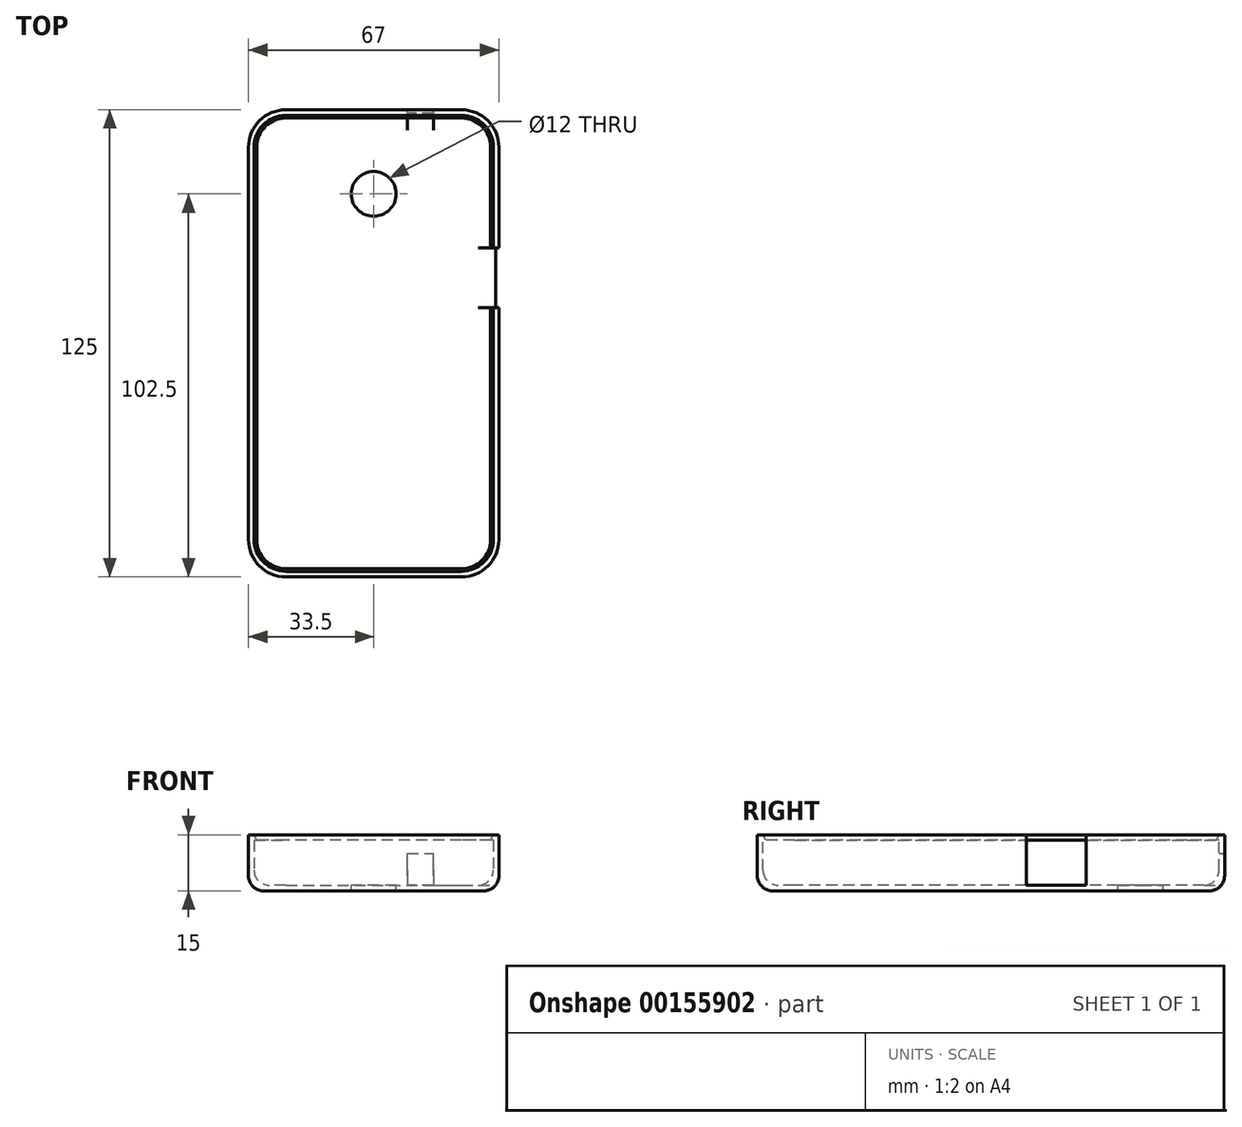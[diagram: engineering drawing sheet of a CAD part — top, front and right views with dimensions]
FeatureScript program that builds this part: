
annotation { "Feature Type Name" : "Feature", "Feature Type Description" : "" }
export const myFeature = defineFeature(function(context is Context, id is Id, definition is map)
    precondition{}
    {
        {
            var Q0;
            Q0=qCreatedBy(makeId("Top.planeOp"),FACE);
            var sketch = newSketch(context, id + "F0", { "sketchPlane" : qUnion([Q0])});
            skLineSegment(sketch, "E0.bottom", {"start": v(-23.5, 62.5) * mm, "end": v(23.5, 62.5) * mm});
            skLineSegment(sketch, "E0.top", {"start": v(-23.5, -62.5) * mm, "end": v(23.5, -62.5) * mm});
            skLineSegment(sketch, "E0.left", {"start": v(-33.5, 52.5) * mm, "end": v(-33.5, -52.5) * mm});
            skLineSegment(sketch, "E0.right", {"start": v(33.5, 52.5) * mm, "end": v(33.5, -52.5) * mm});
            skPoint(sketch, "E1.visualSharp", {"position": v(-33.5, 62.5) * mm});
            skArc(sketch, "E1.filletArc", {"start": v(-23.5, 62.5) * mm, "mid": v(-30.57, 59.57) * mm, "end": v(-33.5, 52.5) * mm});
            skPoint(sketch, "E2.visualSharp", {"position": v(33.5, 62.5) * mm});
            skArc(sketch, "E2.filletArc", {"start": v(33.5, 52.5) * mm, "mid": v(30.57, 59.57) * mm, "end": v(23.5, 62.5) * mm});
            skPoint(sketch, "E3.visualSharp", {"position": v(33.5, -62.5) * mm});
            skArc(sketch, "E3.filletArc", {"start": v(23.5, -62.5) * mm, "mid": v(30.57, -59.57) * mm, "end": v(33.5, -52.5) * mm});
            skPoint(sketch, "E4.visualSharp", {"position": v(-33.5, -62.5) * mm});
            skArc(sketch, "E4.filletArc", {"start": v(-33.5, -52.5) * mm, "mid": v(-30.57, -59.57) * mm, "end": v(-23.5, -62.5) * mm});
            skSolve(sketch);
        }
        {
            var Q0;
            Q0=makeQuery(id+"F0.imprint","IMPRINT",FACE,{"disambiguationData":[TD([[makeQuery(id+"F0.imprint","IMPRINT",EDGE,{"derivedFrom":sQuery(id+"F0.wireOp",EDGE,"E0.bottom")}),-1.0]])]});
            extrude(context, id + "F1", {"entities" : qUnion([Q0]), "depth" : 15 * mm});
        }
        {
            var Q0;
            Q0=makeQuery(id+"F1.opExtrude","CAP_FACE",FACE,{"disambiguationData":[OSD([sQuery(id+"F0.wireOp",EDGE,"E0.bottom"),sQuery(id+"F0.wireOp",EDGE,"E0.top"),sQuery(id+"F0.wireOp",EDGE,"E0.left"),sQuery(id+"F0.wireOp",EDGE,"E0.right"),sQuery(id+"F0.wireOp",EDGE,"E1.filletArc"),sQuery(id+"F0.wireOp",EDGE,"E2.filletArc"),sQuery(id+"F0.wireOp",EDGE,"E3.filletArc"),sQuery(id+"F0.wireOp",EDGE,"E4.filletArc")])],"isStart":false});
            shell(context, id + "F2", {"entities" : qUnion([Q0]), "thickness" : 1.5 * mm});
        }
        {
            var Q0;
            Q0=makeQuery(id+"F2.opShell","OFFSET_FACE",FACE,{"disambiguationData":[OSD([sQuery(id+"F0.wireOp",EDGE,"E0.bottom"),sQuery(id+"F0.wireOp",EDGE,"E0.top"),sQuery(id+"F0.wireOp",EDGE,"E0.left"),sQuery(id+"F0.wireOp",EDGE,"E0.right"),sQuery(id+"F0.wireOp",EDGE,"E1.filletArc"),sQuery(id+"F0.wireOp",EDGE,"E2.filletArc"),sQuery(id+"F0.wireOp",EDGE,"E3.filletArc"),sQuery(id+"F0.wireOp",EDGE,"E4.filletArc")])]});
            var sketch = newSketch(context, id + "F3", { "sketchPlane" : qUnion([Q0])});
            skCircle(sketch, "E5", {"center": v(0, 40) * mm, "radius": 6 * mm});
            skSolve(sketch);
        }
        {
            var Q0;
            Q0=makeQuery(id+"F3.imprint","IMPRINT",FACE,{"disambiguationData":[TD([[makeQuery(id+"F3.imprint","IMPRINT",EDGE,{"derivedFrom":sQuery(id+"F3.wireOp",EDGE,"E5")}),1.0]])]});
            extrude(context, id + "F4", {"entities" : qUnion([Q0]), "operationType" : NewBodyOperationType.REMOVE, "oppositeDirection" : true, "depth" : 25 * mm});
        }
        {
            var Q0;
            {var subQ0=sQuery(id+"F0.wireOp",EDGE,"E0.right");Q0=makeQuery(id+"F2.opShell","OFFSET_EDGE",EDGE,{"disambiguationData":[OSD([subQ0]),TDD([makeQuery(id+"F1.opExtrude","CAP_EDGE",EDGE,{"disambiguationData":[OSD([subQ0])],"isStart":true})])]});}
            var Q1;
            {var subQ0=sQuery(id+"F0.wireOp",EDGE,"E2.filletArc");Q1=makeQuery(id+"F2.opShell","OFFSET_EDGE",EDGE,{"disambiguationData":[OSD([subQ0]),TDD([makeQuery(id+"F1.opExtrude","CAP_EDGE",EDGE,{"disambiguationData":[OSD([subQ0])],"isStart":true})])]});}
            var Q2;
            {var subQ0=sQuery(id+"F0.wireOp",EDGE,"E0.bottom");Q2=makeQuery(id+"F2.opShell","OFFSET_EDGE",EDGE,{"disambiguationData":[OSD([subQ0]),TDD([makeQuery(id+"F1.opExtrude","CAP_EDGE",EDGE,{"disambiguationData":[OSD([subQ0])],"isStart":true})])]});}
            var Q3;
            {var subQ0=sQuery(id+"F0.wireOp",EDGE,"E1.filletArc");Q3=makeQuery(id+"F2.opShell","OFFSET_EDGE",EDGE,{"disambiguationData":[OSD([subQ0]),TDD([makeQuery(id+"F1.opExtrude","CAP_EDGE",EDGE,{"disambiguationData":[OSD([subQ0])],"isStart":true})])]});}
            var Q4;
            {var subQ0=sQuery(id+"F0.wireOp",EDGE,"E0.left");Q4=makeQuery(id+"F2.opShell","OFFSET_EDGE",EDGE,{"disambiguationData":[OSD([subQ0]),TDD([makeQuery(id+"F1.opExtrude","CAP_EDGE",EDGE,{"disambiguationData":[OSD([subQ0])],"isStart":true})])]});}
            var Q5;
            {var subQ0=sQuery(id+"F0.wireOp",EDGE,"E4.filletArc");Q5=makeQuery(id+"F2.opShell","OFFSET_EDGE",EDGE,{"disambiguationData":[OSD([subQ0]),TDD([makeQuery(id+"F1.opExtrude","CAP_EDGE",EDGE,{"disambiguationData":[OSD([subQ0])],"isStart":true})])]});}
            var Q6;
            {var subQ0=sQuery(id+"F0.wireOp",EDGE,"E0.top");Q6=makeQuery(id+"F2.opShell","OFFSET_EDGE",EDGE,{"disambiguationData":[OSD([subQ0]),TDD([makeQuery(id+"F1.opExtrude","CAP_EDGE",EDGE,{"disambiguationData":[OSD([subQ0])],"isStart":true})])]});}
            var Q7;
            {var subQ0=sQuery(id+"F0.wireOp",EDGE,"E3.filletArc");Q7=makeQuery(id+"F2.opShell","OFFSET_EDGE",EDGE,{"disambiguationData":[OSD([subQ0]),TDD([makeQuery(id+"F1.opExtrude","CAP_EDGE",EDGE,{"disambiguationData":[OSD([subQ0])],"isStart":true})])]});}
            fillet(context, id + "F5", {"entities" : qUnion([Q0, Q1, Q2, Q3, Q4, Q5, Q6, Q7]), "radius" : 4 * mm, "tangentPropagation" : true, "allowEdgeOverflow" : false});
        }
        {
            var Q0;
            Q0=makeQuery(id+"F1.opExtrude","CAP_EDGE",EDGE,{"disambiguationData":[OSD([sQuery(id+"F0.wireOp",EDGE,"E0.left")])],"isStart":true});
            var Q1;
            Q1=makeQuery(id+"F1.opExtrude","CAP_EDGE",EDGE,{"disambiguationData":[OSD([sQuery(id+"F0.wireOp",EDGE,"E1.filletArc")])],"isStart":true});
            var Q2;
            Q2=makeQuery(id+"F1.opExtrude","CAP_EDGE",EDGE,{"disambiguationData":[OSD([sQuery(id+"F0.wireOp",EDGE,"E4.filletArc")])],"isStart":true});
            var Q3;
            Q3=makeQuery(id+"F1.opExtrude","CAP_EDGE",EDGE,{"disambiguationData":[OSD([sQuery(id+"F0.wireOp",EDGE,"E0.top")])],"isStart":true});
            var Q4;
            Q4=makeQuery(id+"F1.opExtrude","CAP_EDGE",EDGE,{"disambiguationData":[OSD([sQuery(id+"F0.wireOp",EDGE,"E3.filletArc")])],"isStart":true});
            var Q5;
            Q5=makeQuery(id+"F1.opExtrude","CAP_EDGE",EDGE,{"disambiguationData":[OSD([sQuery(id+"F0.wireOp",EDGE,"E0.right")])],"isStart":true});
            var Q6;
            Q6=makeQuery(id+"F1.opExtrude","CAP_EDGE",EDGE,{"disambiguationData":[OSD([sQuery(id+"F0.wireOp",EDGE,"E0.bottom")])],"isStart":true});
            var Q7;
            Q7=makeQuery(id+"F1.opExtrude","CAP_EDGE",EDGE,{"disambiguationData":[OSD([sQuery(id+"F0.wireOp",EDGE,"E2.filletArc")])],"isStart":true});
            fillet(context, id + "F6", {"entities" : qUnion([Q0, Q1, Q2, Q3, Q4, Q5, Q6, Q7]), "radius" : 4 * mm, "tangentPropagation" : true, "allowEdgeOverflow" : false});
        }
        {
            var Q0;
            Q0=makeQuery(id+"F1.opExtrude","SWEPT_FACE",FACE,{"disambiguationData":[OSD([sQuery(id+"F0.wireOp",EDGE,"E0.right")])]});
            var sketch = newSketch(context, id + "F7", { "sketchPlane" : qUnion([Q0])});
            skLineSegment(sketch, "E6", {"start": v(52.5, 9.5) * mm, "end": v(25.5, 9.5) * mm});
            skLineSegment(sketch, "E7", {"start": v(9.5, 15) * mm, "end": v(25.5, 15) * mm});
            skLineSegment(sketch, "E8", {"start": v(25.5, 15) * mm, "end": v(25.5, 1.5) * mm});
            skLineSegment(sketch, "E9", {"start": v(25.5, 1.5) * mm, "end": v(9.5, 1.5) * mm});
            skLineSegment(sketch, "E10", {"start": v(9.5, 1.5) * mm, "end": v(9.5, 15) * mm});
            skSolve(sketch);
        }
        {
            var Q0;
            Q0=qCreatedBy(makeId("Front.planeOp"),FACE);
            cPlane(context, id + "F8", {"entities" : qUnion([Q0]), "cplaneType" : CPlaneType.OFFSET, "offset" : 52.5 * mm, "width" : 150 * mm, "height" : 150 * mm});
        }
        {
            var Q0;
            Q0=qCreatedBy(id+"F8.planeOp",FACE);
            var sketch = newSketch(context, id + "F9", { "sketchPlane" : qUnion([Q0])});
            skLineSegment(sketch, "E11", {"start": v(32, 15) * mm, "end": v(32, 13.5) * mm});
            skLineSegment(sketch, "E12", {"start": v(32, 13.5) * mm, "end": v(31.3, 13.5) * mm});
            skLineSegment(sketch, "E13", {"start": v(31.3, 13.5) * mm, "end": v(32, 15) * mm});
            skSolve(sketch);
        }
        {
            var Q0;
            Q0 = qSketchRegion(id + "F9", true);
            var Q1;
            {var subQ0=sQuery(id+"F0.wireOp",EDGE,"E0.right");Q1=makeQuery(id+"F2.opShell","OFFSET_EDGE",EDGE,{"disambiguationData":[OSD([subQ0]),TDD([makeQuery(id+"F1.opExtrude","CAP_EDGE",EDGE,{"disambiguationData":[OSD([subQ0])],"isStart":false})])]});}
            var Q2;
            {var subQ0=sQuery(id+"F0.wireOp",EDGE,"E2.filletArc");Q2=makeQuery(id+"F2.opShell","OFFSET_EDGE",EDGE,{"disambiguationData":[OSD([subQ0]),TDD([makeQuery(id+"F1.opExtrude","CAP_EDGE",EDGE,{"disambiguationData":[OSD([subQ0])],"isStart":false})])]});}
            var Q3;
            {var subQ0=sQuery(id+"F0.wireOp",EDGE,"E0.bottom");Q3=makeQuery(id+"F2.opShell","OFFSET_EDGE",EDGE,{"disambiguationData":[OSD([subQ0]),TDD([makeQuery(id+"F1.opExtrude","CAP_EDGE",EDGE,{"disambiguationData":[OSD([subQ0])],"isStart":false})])]});}
            var Q4;
            {var subQ0=sQuery(id+"F0.wireOp",EDGE,"E1.filletArc");Q4=makeQuery(id+"F2.opShell","OFFSET_EDGE",EDGE,{"disambiguationData":[OSD([subQ0]),TDD([makeQuery(id+"F1.opExtrude","CAP_EDGE",EDGE,{"disambiguationData":[OSD([subQ0])],"isStart":false})])]});}
            var Q5;
            {var subQ0=sQuery(id+"F0.wireOp",EDGE,"E0.left");Q5=makeQuery(id+"F2.opShell","OFFSET_EDGE",EDGE,{"disambiguationData":[OSD([subQ0]),TDD([makeQuery(id+"F1.opExtrude","CAP_EDGE",EDGE,{"disambiguationData":[OSD([subQ0])],"isStart":false})])]});}
            var Q6;
            {var subQ0=sQuery(id+"F0.wireOp",EDGE,"E4.filletArc");Q6=makeQuery(id+"F2.opShell","OFFSET_EDGE",EDGE,{"disambiguationData":[OSD([subQ0]),TDD([makeQuery(id+"F1.opExtrude","CAP_EDGE",EDGE,{"disambiguationData":[OSD([subQ0])],"isStart":false})])]});}
            var Q7;
            {var subQ0=sQuery(id+"F0.wireOp",EDGE,"E0.top");Q7=makeQuery(id+"F2.opShell","OFFSET_EDGE",EDGE,{"disambiguationData":[OSD([subQ0]),TDD([makeQuery(id+"F1.opExtrude","CAP_EDGE",EDGE,{"disambiguationData":[OSD([subQ0])],"isStart":false})])]});}
            sweep(context, id + "F10", {"operationType" : NewBodyOperationType.ADD, "profiles" : qUnion([Q0]), "path" : qUnion([Q1, Q2, Q3, Q4, Q5, Q6, Q7])});
        }
        {
            var Q0;
            Q0 = qSketchRegion(id + "F9", true);
            var Q1;
            {var subQ0=sQuery(id+"F0.wireOp",EDGE,"E3.filletArc");Q1=makeQuery(id+"F2.opShell","OFFSET_EDGE",EDGE,{"disambiguationData":[OSD([subQ0]),TDD([makeQuery(id+"F1.opExtrude","CAP_EDGE",EDGE,{"disambiguationData":[OSD([subQ0])],"isStart":false})])]});}
            sweep(context, id + "F11", {"operationType" : NewBodyOperationType.ADD, "profiles" : qUnion([Q0]), "path" : qUnion([Q1])});
        }
        {
            var Q0;
            Q0 = qSketchRegion(id + "F7", true);
            extrude(context, id + "F12", {"entities" : qUnion([Q0]), "operationType" : NewBodyOperationType.REMOVE, "oppositeDirection" : true, "depth" : 7 * mm});
        }
        {
            var Q0;
            Q0=makeQuery(id+"F1.opExtrude","SWEPT_FACE",FACE,{"disambiguationData":[OSD([sQuery(id+"F0.wireOp",EDGE,"E0.bottom")])]});
            var sketch = newSketch(context, id + "F13", { "sketchPlane" : qUnion([Q0])});
            skLineSegment(sketch, "E14", {"start": v(-23.5, 9.5) * mm, "end": v(-16, 9.5) * mm});
            skLineSegment(sketch, "E15", {"start": v(-16, 1.5) * mm, "end": v(-16, 15) * mm});
            skLineSegment(sketch, "E16", {"start": v(-16, 1.5) * mm, "end": v(-9, 1.5) * mm});
            skLineSegment(sketch, "E17", {"start": v(-9, 1.5) * mm, "end": v(-9, 10) * mm});
            skLineSegment(sketch, "E18", {"start": v(-9, 10) * mm, "end": v(-16, 10) * mm});
            skSolve(sketch);
        }
        {
            var Q0;
            {var subQ0=sQuery(id+"F13.wireOp",EDGE,"E18");Q0=makeQuery(id+"F13.imprint","IMPRINT",FACE,{"disambiguationData":[TD([[makeQuery(id+"F13.imprint","IMPRINT",EDGE,{"derivedFrom":subQ0}),1.0]])]});}
            var Q1;
            {var subQ0=sQuery(id+"F13.wireOp",EDGE,"E16");Q1=makeQuery(id+"F13.imprint","IMPRINT",FACE,{"disambiguationData":[TD([[makeQuery(id+"F13.imprint","IMPRINT",EDGE,{"derivedFrom":subQ0}),1.0]])]});}
            extrude(context, id + "F14", {"entities" : qUnion([Q0, Q1]), "operationType" : NewBodyOperationType.REMOVE, "oppositeDirection" : true, "depth" : 25 * mm});
        }
    });
